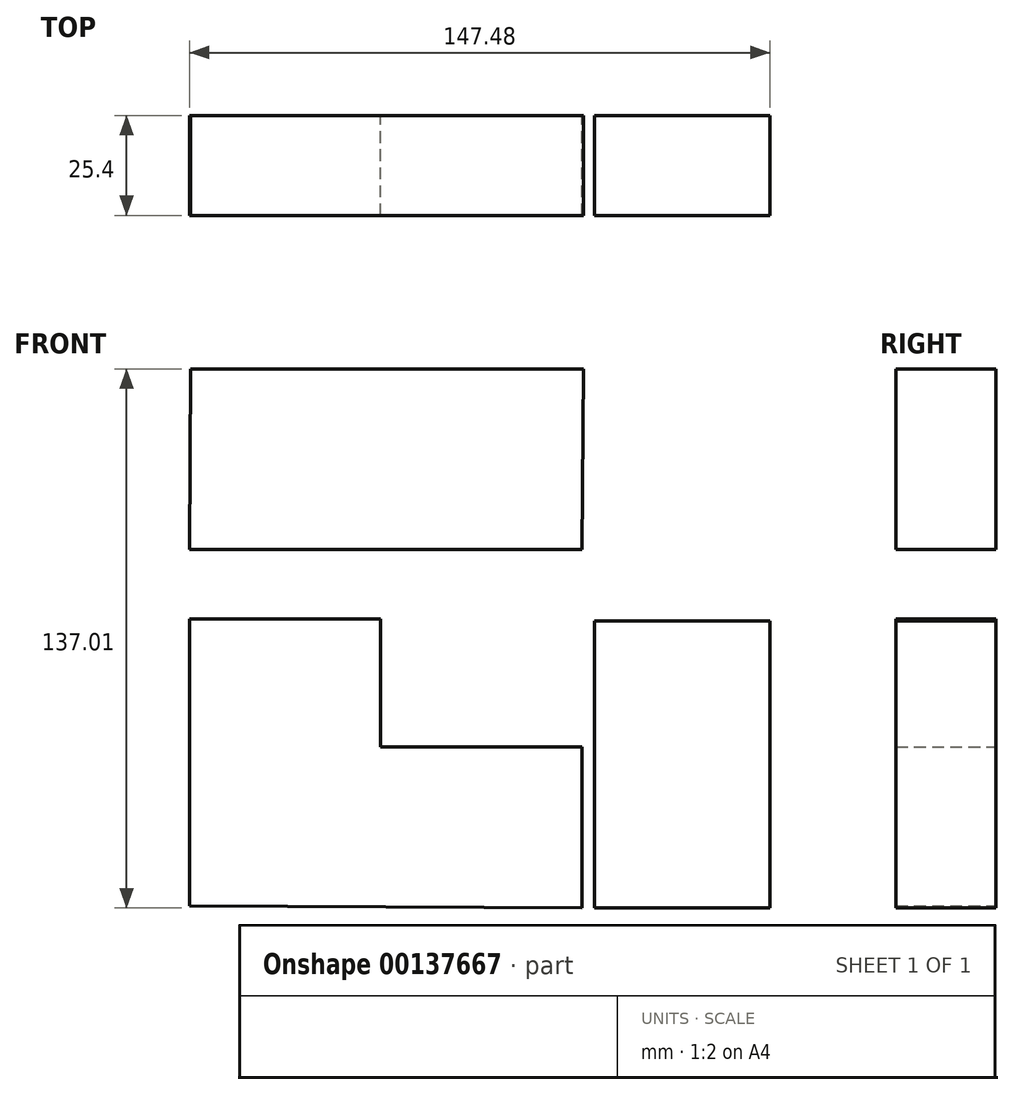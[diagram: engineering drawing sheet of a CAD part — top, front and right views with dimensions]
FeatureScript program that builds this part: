
annotation { "Feature Type Name" : "Feature", "Feature Type Description" : "" }
export const myFeature = defineFeature(function(context is Context, id is Id, definition is map)
    precondition{}
    {
        {
            var Q0;
            Q0=qCreatedBy(makeId("Front.planeOp"),FACE);
            var sketch = newSketch(context, id + "F0", { "sketchPlane" : qUnion([Q0])});
            skLineSegment(sketch, "E0", {"start": v(-76.37, -2.26) * mm, "end": v(-27.95, -2.26) * mm});
            skLineSegment(sketch, "E1", {"start": v(-27.95, -2.26) * mm, "end": v(-27.95, -34.74) * mm});
            skLineSegment(sketch, "E2", {"start": v(-27.95, -34.74) * mm, "end": v(23.23, -34.74) * mm});
            skLineSegment(sketch, "E3", {"start": v(-76.37, -2.26) * mm, "end": v(-76.37, -75.09) * mm});
            skLineSegment(sketch, "E4", {"start": v(23.23, -34.74) * mm, "end": v(23.23, -75.68) * mm});
            skLineSegment(sketch, "E5", {"start": v(23.23, -75.68) * mm, "end": v(-76.37, -75.09) * mm});
            skSolve(sketch);
        }
        {
            var Q0;
            Q0 = qSketchRegion(id + "F0", true);
            extrude(context, id + "F1", {"entities" : qUnion([Q0]), "depth" : 25.4 * mm});
        }
        {
            var Q0;
            Q0=qCreatedBy(makeId("Front.planeOp"),FACE);
            var sketch = newSketch(context, id + "F2", { "sketchPlane" : qUnion([Q0])});
            skLineSegment(sketch, "E6", {"start": v(-76.13, 61.31) * mm, "end": v(23.62, 61.31) * mm});
            skLineSegment(sketch, "E7", {"start": v(-76.44, 15.43) * mm, "end": v(23.32, 15.43) * mm});
            skLineSegment(sketch, "E8", {"start": v(23.62, 61.31) * mm, "end": v(23.32, 15.43) * mm});
            skLineSegment(sketch, "E9", {"start": v(-76.13, 61.31) * mm, "end": v(-76.44, 15.43) * mm});
            skSolve(sketch);
        }
        {
            var Q0;
            Q0=makeQuery(id+"F2.imprint","IMPRINT",FACE,{"disambiguationData":[TD([[makeQuery(id+"F2.imprint","IMPRINT",EDGE,{"derivedFrom":sQuery(id+"F2.wireOp",EDGE,"E6")}),-1.0]])]});
            extrude(context, id + "F3", {"entities" : qUnion([Q0]), "depth" : 25.4 * mm});
        }
        {
            var Q0;
            Q0=qCreatedBy(makeId("Front.planeOp"),FACE);
            var sketch = newSketch(context, id + "F4", { "sketchPlane" : qUnion([Q0])});
            skLineSegment(sketch, "E10", {"start": v(26.4, -75.7) * mm, "end": v(26.4, -2.73) * mm});
            skLineSegment(sketch, "E11", {"start": v(26.4, -2.73) * mm, "end": v(71.04, -2.73) * mm});
            skLineSegment(sketch, "E12", {"start": v(71.04, -2.73) * mm, "end": v(71.04, -75.7) * mm});
            skLineSegment(sketch, "E13", {"start": v(71.04, -75.7) * mm, "end": v(26.4, -75.7) * mm});
            skSolve(sketch);
        }
        {
            var Q0;
            Q0=makeQuery(id+"F4.imprint","IMPRINT",FACE,{"disambiguationData":[TD([[makeQuery(id+"F4.imprint","IMPRINT",EDGE,{"derivedFrom":sQuery(id+"F4.wireOp",EDGE,"E10")}),-1.0]])]});
            extrude(context, id + "F5", {"entities" : qUnion([Q0]), "depth" : 25.4 * mm});
        }
    });
